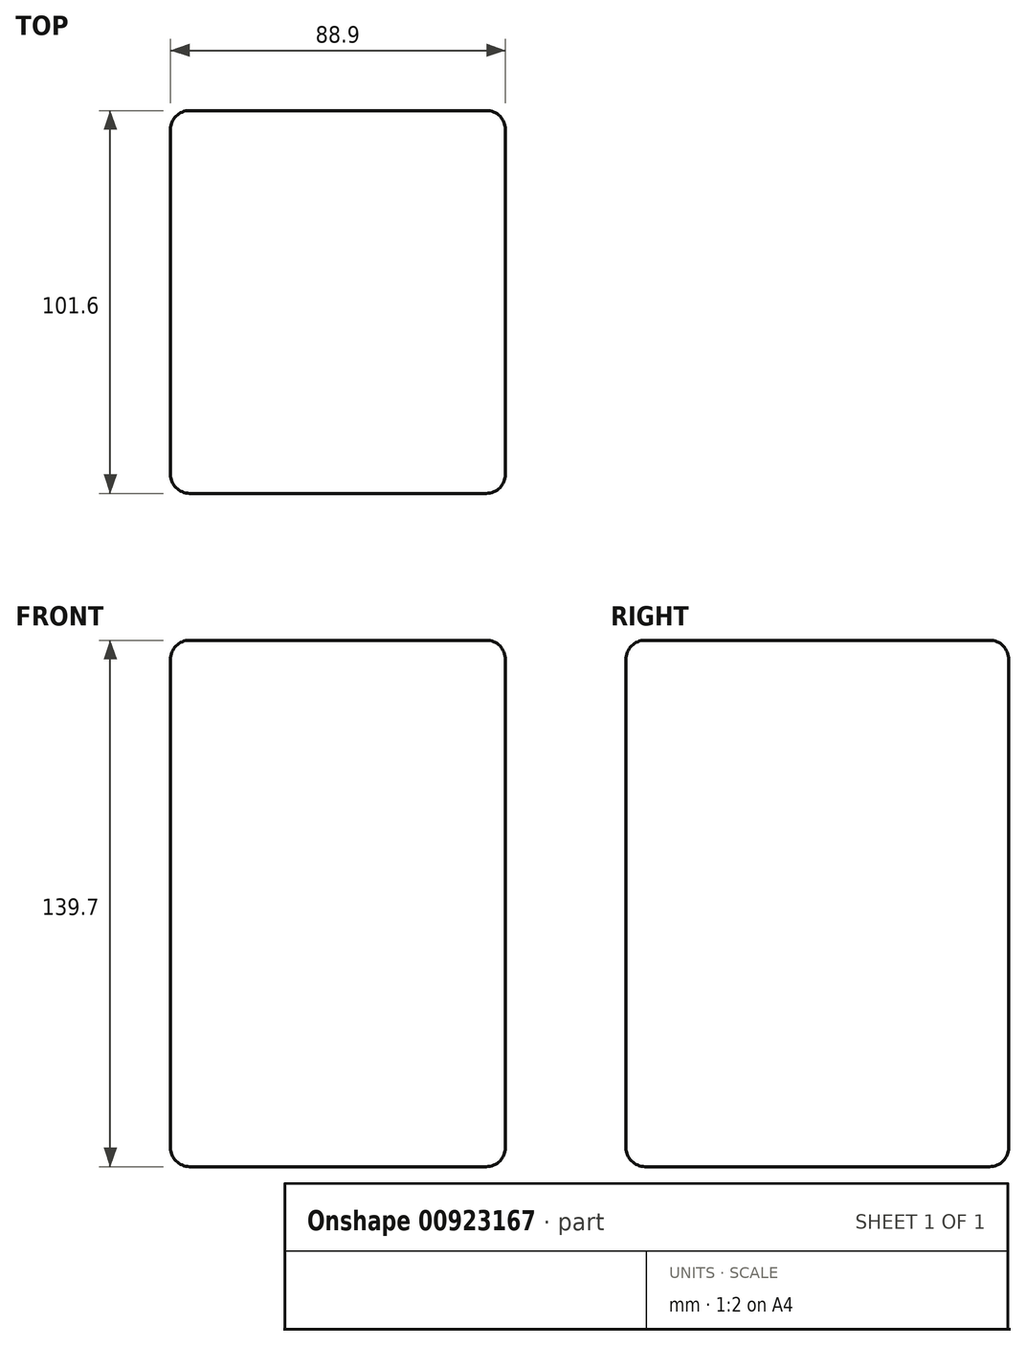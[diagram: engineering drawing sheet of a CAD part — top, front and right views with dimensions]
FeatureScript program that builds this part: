
annotation { "Feature Type Name" : "Feature", "Feature Type Description" : "" }
export const myFeature = defineFeature(function(context is Context, id is Id, definition is map)
    precondition{}
    {
        {
            var Q0;
            Q0=qCreatedBy(makeId("Front.planeOp"),FACE);
            var sketch = newSketch(context, id + "F0", { "sketchPlane" : qUnion([Q0])});
            skLineSegment(sketch, "E0.bottom", {"start": v(-44.45, 69.85) * mm, "end": v(44.45, 69.85) * mm});
            skLineSegment(sketch, "E0.top", {"start": v(-44.45, -69.85) * mm, "end": v(44.45, -69.85) * mm});
            skLineSegment(sketch, "E0.left", {"start": v(-44.45, 69.85) * mm, "end": v(-44.45, -69.85) * mm});
            skLineSegment(sketch, "E0.right", {"start": v(44.45, 69.85) * mm, "end": v(44.45, -69.85) * mm});
            skPoint(sketch, "E0.middle", {"position": v(0, 0) * mm});
            skSolve(sketch);
        }
        {
            var Q0;
            Q0=makeQuery(id+"F0.imprint","IMPRINT",FACE,{"disambiguationData":[TD([[makeQuery(id+"F0.imprint","IMPRINT",EDGE,{"derivedFrom":sQuery(id+"F0.wireOp",EDGE,"E0.bottom")}),-1.0]])]});
            extrude(context, id + "F1", {"entities" : qUnion([Q0]), "endBound" : BoundingType.SYMMETRIC, "depth" : 101.6 * mm, "offsetDistance" : 25.4 * mm});
        }
        {
            var Q0;
            Q0=makeQuery(id+"F1.opExtrude","CAP_EDGE",EDGE,{"disambiguationData":[OSD([sQuery(id+"F0.wireOp",EDGE,"E0.bottom")])],"isStart":false});
            var Q1;
            Q1=makeQuery(id+"F1.opExtrude","CAP_EDGE",EDGE,{"disambiguationData":[OSD([sQuery(id+"F0.wireOp",EDGE,"E0.right")])],"isStart":false});
            var Q2;
            Q2=makeQuery(id+"F1.opExtrude","SWEPT_EDGE",EDGE,{"disambiguationData":[OSD([sQuery(id+"F0.wireOp",EDGE,"E0.bottom"),sQuery(id+"F0.wireOp",EDGE,"E0.right")])]});
            var Q3;
            Q3=makeQuery(id+"F1.opExtrude","CAP_EDGE",EDGE,{"disambiguationData":[OSD([sQuery(id+"F0.wireOp",EDGE,"E0.bottom")])],"isStart":true});
            var Q4;
            Q4=makeQuery(id+"F1.opExtrude","SWEPT_EDGE",EDGE,{"disambiguationData":[OSD([sQuery(id+"F0.wireOp",EDGE,"E0.bottom"),sQuery(id+"F0.wireOp",EDGE,"E0.left")])]});
            var Q5;
            Q5=makeQuery(id+"F1.opExtrude","CAP_EDGE",EDGE,{"disambiguationData":[OSD([sQuery(id+"F0.wireOp",EDGE,"E0.left")])],"isStart":false});
            var Q6;
            Q6=makeQuery(id+"F1.opExtrude","CAP_EDGE",EDGE,{"disambiguationData":[OSD([sQuery(id+"F0.wireOp",EDGE,"E0.right")])],"isStart":true});
            var Q7;
            Q7=makeQuery(id+"F1.opExtrude","CAP_EDGE",EDGE,{"disambiguationData":[OSD([sQuery(id+"F0.wireOp",EDGE,"E0.top")])],"isStart":false});
            var Q8;
            Q8=makeQuery(id+"F1.opExtrude","SWEPT_EDGE",EDGE,{"disambiguationData":[OSD([sQuery(id+"F0.wireOp",EDGE,"E0.top"),sQuery(id+"F0.wireOp",EDGE,"E0.left")])]});
            var Q9;
            Q9=makeQuery(id+"F1.opExtrude","CAP_EDGE",EDGE,{"disambiguationData":[OSD([sQuery(id+"F0.wireOp",EDGE,"E0.top")])],"isStart":true});
            var Q10;
            Q10=makeQuery(id+"F1.opExtrude","SWEPT_EDGE",EDGE,{"disambiguationData":[OSD([sQuery(id+"F0.wireOp",EDGE,"E0.top"),sQuery(id+"F0.wireOp",EDGE,"E0.right")])]});
            var Q11;
            Q11=makeQuery(id+"F1.opExtrude","CAP_EDGE",EDGE,{"disambiguationData":[OSD([sQuery(id+"F0.wireOp",EDGE,"E0.left")])],"isStart":true});
            fillet(context, id + "F2", {"entities" : qUnion([Q0, Q1, Q2, Q3, Q4, Q5, Q6, Q7, Q8, Q9, Q10, Q11]), "radius" : 5.08 * mm, "tangentPropagation" : true, "allowEdgeOverflow" : false});
        }
    });
